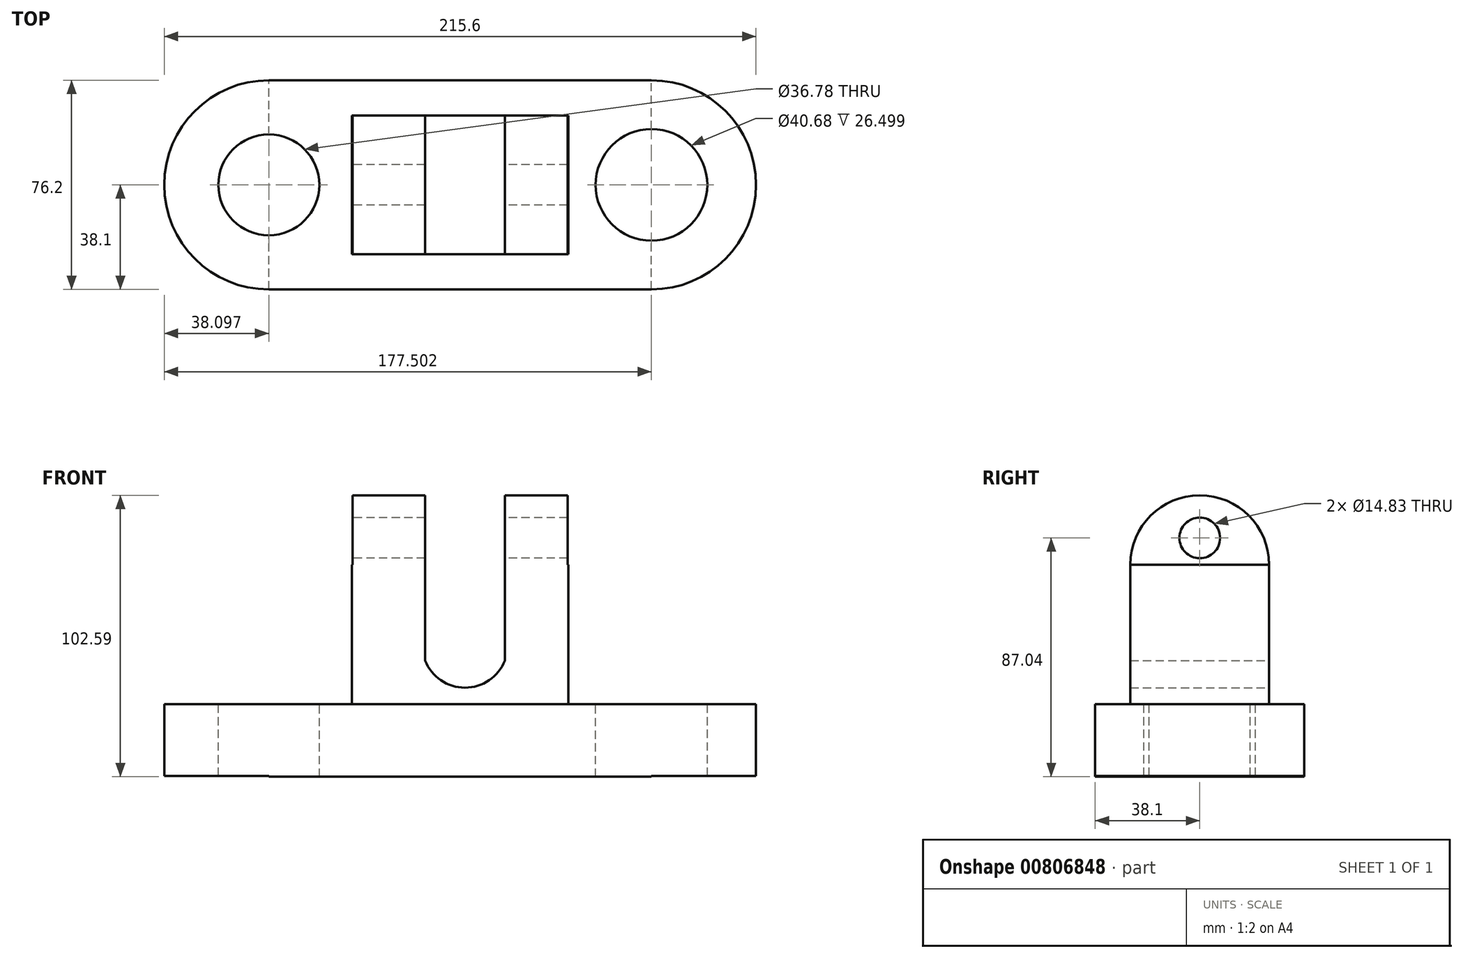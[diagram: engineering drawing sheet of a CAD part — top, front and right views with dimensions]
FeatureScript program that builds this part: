
annotation { "Feature Type Name" : "Feature", "Feature Type Description" : "" }
export const myFeature = defineFeature(function(context is Context, id is Id, definition is map)
    precondition{}
    {
        {
            var Q0;
            Q0=qCreatedBy(makeId("Front.planeOp"),FACE);
            var sketch = newSketch(context, id + "F0", { "sketchPlane" : qUnion([Q0])});
            skLineSegment(sketch, "E0.bottom", {"start": v(-69.7, 13.25) * mm, "end": v(69.7, 13.25) * mm});
            skLineSegment(sketch, "E0.top", {"start": v(-69.7, -13.25) * mm, "end": v(69.7, -13.25) * mm});
            skLineSegment(sketch, "E0.left", {"start": v(-69.7, 13.25) * mm, "end": v(-69.7, -13.25) * mm});
            skLineSegment(sketch, "E0.right", {"start": v(69.7, 13.25) * mm, "end": v(69.7, -13.25) * mm});
            skPoint(sketch, "E0.middle", {"position": v(0, 0) * mm});
            skSolve(sketch);
        }
        {
            var Q0;
            Q0 = qSketchRegion(id + "F0", true);
            extrude(context, id + "F1", {"entities" : qUnion([Q0]), "endBound" : BoundingType.SYMMETRIC, "depth" : 76.2 * mm, "offsetDistance" : 25.4 * mm});
        }
        {
            var Q0;
            Q0=makeQuery(id+"F1.opExtrude","SWEPT_FACE",FACE,{"disambiguationData":[OSD([sQuery(id+"F0.wireOp",EDGE,"E0.bottom")])]});
            var sketch = newSketch(context, id + "F2", { "sketchPlane" : qUnion([Q0])});
            skArc(sketch, "E1", {"start": v(69.7, -38.1) * mm, "mid": v(107.8, 0) * mm, "end": v(69.7, 38.1) * mm});
            skSolve(sketch);
        }
        {
            var Q0;
            Q0=makeQuery(id+"F2.imprint","IMPRINT",FACE,{"disambiguationData":[TD([[makeQuery(id+"F2.imprint","IMPRINT",EDGE,{"derivedFrom":sQuery(id+"F2.wireOp",EDGE,"E1")}),1.0]])]});
            extrude(context, id + "F3", {"entities" : qUnion([Q0]), "operationType" : NewBodyOperationType.ADD, "oppositeDirection" : true, "depth" : 26.16 * mm, "offsetDistance" : 25.4 * mm});
        }
        {
            var Q0;
            {var subQ0=sQuery(id+"F0.wireOp",EDGE,"E0.bottom");Q0=makeQuery(id+"F3.boolean.opBoolean","MERGE",FACE,{"derivedFrom":[makeQuery(id+"F1.opExtrude","SWEPT_FACE",FACE,{"disambiguationData":[OSD([subQ0])]}),makeQuery(id+"F3.opExtrude","CAP_FACE",FACE,{"disambiguationData":[OSD([subQ0,sQuery(id+"F0.wireOp",EDGE,"E0.right"),sQuery(id+"F2.wireOp",EDGE,"E1")])],"isStart":true})]});}
            var sketch = newSketch(context, id + "F4", { "sketchPlane" : qUnion([Q0])});
            skArc(sketch, "E2", {"start": v(-69.7, 38.1) * mm, "mid": v(-107.8, 0) * mm, "end": v(-69.7, -38.1) * mm});
            skSolve(sketch);
        }
        {
            var Q0;
            Q0=makeQuery(id+"F4.imprint","IMPRINT",FACE,{"disambiguationData":[TD([[makeQuery(id+"F4.imprint","IMPRINT",EDGE,{"derivedFrom":sQuery(id+"F4.wireOp",EDGE,"E2")}),1.0]])]});
            extrude(context, id + "F5", {"entities" : qUnion([Q0]), "operationType" : NewBodyOperationType.ADD, "oppositeDirection" : true, "depth" : 26.16 * mm, "offsetDistance" : 25.4 * mm});
        }
        {
            var Q0;
            {var subQ0=sQuery(id+"F0.wireOp",EDGE,"E0.bottom");Q0=makeQuery(id+"F5.boolean.opBoolean","MERGE",FACE,{"derivedFrom":[makeQuery(id+"F3.boolean.opBoolean","MERGE",FACE,{"derivedFrom":[makeQuery(id+"F1.opExtrude","SWEPT_FACE",FACE,{"disambiguationData":[OSD([subQ0])]}),makeQuery(id+"F3.opExtrude","CAP_FACE",FACE,{"disambiguationData":[OSD([subQ0,sQuery(id+"F0.wireOp",EDGE,"E0.right"),sQuery(id+"F2.wireOp",EDGE,"E1")])],"isStart":true})]}),makeQuery(id+"F5.opExtrude","CAP_FACE",FACE,{"disambiguationData":[OSD([subQ0,sQuery(id+"F0.wireOp",EDGE,"E0.left"),sQuery(id+"F4.wireOp",EDGE,"E2")])],"isStart":true})]});}
            var sketch = newSketch(context, id + "F6", { "sketchPlane" : qUnion([Q0])});
            skCircle(sketch, "E3", {"center": v(69.7, 0) * mm, "radius": 20.34 * mm});
            skCircle(sketch, "E4", {"center": v(-69.7, 0) * mm, "radius": 18.4 * mm});
            skSolve(sketch);
        }
        {
            var Q0;
            Q0 = qSketchRegion(id + "F6", true);
            extrude(context, id + "F7", {"entities" : qUnion([Q0]), "operationType" : NewBodyOperationType.REMOVE, "endBound" : BoundingType.THROUGH_ALL, "oppositeDirection" : true, "depth" : 25.4 * mm, "offsetDistance" : 25.4 * mm});
        }
        {
            var Q0;
            {var subQ0=sQuery(id+"F0.wireOp",EDGE,"E0.bottom");Q0=makeQuery(id+"F5.boolean.opBoolean","MERGE",FACE,{"derivedFrom":[makeQuery(id+"F3.boolean.opBoolean","MERGE",FACE,{"derivedFrom":[makeQuery(id+"F1.opExtrude","SWEPT_FACE",FACE,{"disambiguationData":[OSD([subQ0])]}),makeQuery(id+"F3.opExtrude","CAP_FACE",FACE,{"disambiguationData":[OSD([subQ0,sQuery(id+"F0.wireOp",EDGE,"E0.right"),sQuery(id+"F2.wireOp",EDGE,"E1")])],"isStart":true})]}),makeQuery(id+"F5.opExtrude","CAP_FACE",FACE,{"disambiguationData":[OSD([subQ0,sQuery(id+"F0.wireOp",EDGE,"E0.left"),sQuery(id+"F4.wireOp",EDGE,"E2")])],"isStart":true})]});}
            var sketch = newSketch(context, id + "F8", { "sketchPlane" : qUnion([Q0])});
            skLineSegment(sketch, "E5.bottom", {"start": v(39.4, -25.29) * mm, "end": v(-39.4, -25.29) * mm});
            skLineSegment(sketch, "E5.top", {"start": v(39.4, 25.29) * mm, "end": v(-39.4, 25.29) * mm});
            skLineSegment(sketch, "E5.left", {"start": v(39.4, -25.29) * mm, "end": v(39.4, 25.29) * mm});
            skLineSegment(sketch, "E5.right", {"start": v(-39.4, -25.29) * mm, "end": v(-39.4, 25.29) * mm});
            skPoint(sketch, "E5.middle", {"position": v(0, 0) * mm});
            skSolve(sketch);
        }
        {
            var Q0;
            Q0=makeQuery(id+"F8.imprint","IMPRINT",FACE,{"disambiguationData":[TD([[makeQuery(id+"F8.imprint","IMPRINT",EDGE,{"derivedFrom":sQuery(id+"F8.wireOp",EDGE,"E5.bottom")}),-1.0]])]});
            extrude(context, id + "F9", {"entities" : qUnion([Q0]), "operationType" : NewBodyOperationType.ADD, "depth" : 50.8 * mm, "offsetDistance" : 25.4 * mm});
        }
        {
            var Q0;
            Q0=makeQuery(id+"F9.opExtrude","SWEPT_FACE",FACE,{"disambiguationData":[OSD([sQuery(id+"F8.wireOp",EDGE,"E5.top")])]});
            var sketch = newSketch(context, id + "F10", { "sketchPlane" : qUnion([Q0])});
            skLineSegment(sketch, "E6", {"start": v(-16.27, 64.05) * mm, "end": v(-16.27, 29.14) * mm});
            skLineSegment(sketch, "E7", {"start": v(-16.27, 29.14) * mm, "end": v(12.76, 29.14) * mm});
            skLineSegment(sketch, "E8", {"start": v(12.76, 29.14) * mm, "end": v(12.76, 64.05) * mm});
            skArc(sketch, "E9", {"start": v(-16.27, 29.14) * mm, "mid": v(-1.76, 19.2) * mm, "end": v(12.76, 29.14) * mm});
            skSolve(sketch);
        }
        {
            var Q0;
            Q0=makeQuery(id+"F10.imprint","IMPRINT",FACE,{"disambiguationData":[TD([[makeQuery(id+"F10.imprint","IMPRINT",EDGE,{"derivedFrom":sQuery(id+"F10.wireOp",EDGE,"E7")}),-1.0]])]});
            extrude(context, id + "F11", {"entities" : qUnion([Q0]), "operationType" : NewBodyOperationType.REMOVE, "endBound" : BoundingType.THROUGH_ALL, "oppositeDirection" : true, "depth" : 76.2 * mm, "offsetDistance" : 25.4 * mm});
        }
        {
            var Q0;
            Q0=makeQuery(id+"F9.opExtrude","SWEPT_FACE",FACE,{"disambiguationData":[OSD([sQuery(id+"F8.wireOp",EDGE,"E5.top")])]});
            var sketch = newSketch(context, id + "F12", { "sketchPlane" : qUnion([Q0])});
            skLineSegment(sketch, "E10", {"start": v(-16.27, 64.05) * mm, "end": v(-16.27, 29.14) * mm});
            skLineSegment(sketch, "E11", {"start": v(-16.27, 29.14) * mm, "end": v(12.76, 29.14) * mm});
            skLineSegment(sketch, "E12", {"start": v(12.76, 29.14) * mm, "end": v(12.76, 64.05) * mm});
            skLineSegment(sketch, "E13", {"start": v(12.76, 64.05) * mm, "end": v(-16.27, 64.05) * mm});
            skSolve(sketch);
        }
        {
            var Q0;
            Q0=makeQuery(id+"F12.imprint","IMPRINT",FACE,{"disambiguationData":[TD([[makeQuery(id+"F12.imprint","IMPRINT",EDGE,{"derivedFrom":sQuery(id+"F12.wireOp",EDGE,"E10")}),1.0]])]});
            extrude(context, id + "F13", {"entities" : qUnion([Q0]), "operationType" : NewBodyOperationType.REMOVE, "endBound" : BoundingType.THROUGH_ALL, "oppositeDirection" : true, "depth" : 25.4 * mm, "offsetDistance" : 25.4 * mm});
        }
        {
            var Q0;
            Q0=makeQuery(id+"F13.boolean.opBoolean","COPY",FACE,{"derivedFrom":makeQuery(id+"F13.opExtrude","SWEPT_FACE",FACE,{"disambiguationData":[OSD([sQuery(id+"F12.wireOp",EDGE,"E10")])]})});
            var sketch = newSketch(context, id + "F14", { "sketchPlane" : qUnion([Q0])});
            skArc(sketch, "E14", {"start": v(25.29, 64.05) * mm, "mid": v(0, 89.34) * mm, "end": v(-25.29, 64.05) * mm});
            skSolve(sketch);
        }
        {
            var Q0;
            Q0=makeQuery(id+"F14.imprint","IMPRINT",FACE,{"disambiguationData":[TD([[makeQuery(id+"F14.imprint","IMPRINT",EDGE,{"derivedFrom":sQuery(id+"F14.wireOp",EDGE,"E14")}),1.0]])]});
            extrude(context, id + "F15", {"entities" : qUnion([Q0]), "operationType" : NewBodyOperationType.ADD, "oppositeDirection" : true, "depth" : 22.86 * mm, "offsetDistance" : 25.4 * mm});
        }
        {
            var Q0;
            Q0=makeQuery(id+"F13.boolean.opBoolean","COPY",FACE,{"derivedFrom":makeQuery(id+"F13.opExtrude","SWEPT_FACE",FACE,{"disambiguationData":[OSD([sQuery(id+"F12.wireOp",EDGE,"E12")])]})});
            var sketch = newSketch(context, id + "F16", { "sketchPlane" : qUnion([Q0])});
            skArc(sketch, "E15", {"start": v(25.29, 64.05) * mm, "mid": v(0, 89.34) * mm, "end": v(-25.29, 64.05) * mm});
            skSolve(sketch);
        }
        {
            var Q0;
            Q0=makeQuery(id+"F16.imprint","IMPRINT",FACE,{"disambiguationData":[TD([[makeQuery(id+"F16.imprint","IMPRINT",EDGE,{"derivedFrom":sQuery(id+"F16.wireOp",EDGE,"E15")}),1.0]])]});
            extrude(context, id + "F17", {"entities" : qUnion([Q0]), "operationType" : NewBodyOperationType.ADD, "oppositeDirection" : true, "depth" : 26.42 * mm, "offsetDistance" : 25.4 * mm});
        }
        {
            var Q0;
            Q0=makeQuery(id+"F17.opExtrude","CAP_FACE",FACE,{"disambiguationData":[OSD([sQuery(id+"F8.wireOp",EDGE,"E5.top"),sQuery(id+"F12.wireOp",EDGE,"E12"),sQuery(id+"F12.wireOp",EDGE,"E13"),sQuery(id+"F16.wireOp",EDGE,"E15")])],"isStart":false});
            var sketch = newSketch(context, id + "F18", { "sketchPlane" : qUnion([Q0])});
            skCircle(sketch, "E16", {"center": v(0, 73.79) * mm, "radius": 7.42 * mm});
            skSolve(sketch);
        }
        {
            var Q0;
            Q0 = qSketchRegion(id + "F18", true);
            extrude(context, id + "F19", {"entities" : qUnion([Q0]), "operationType" : NewBodyOperationType.REMOVE, "endBound" : BoundingType.THROUGH_ALL, "oppositeDirection" : true, "depth" : 25.4 * mm, "offsetDistance" : 25.4 * mm});
        }
    });
